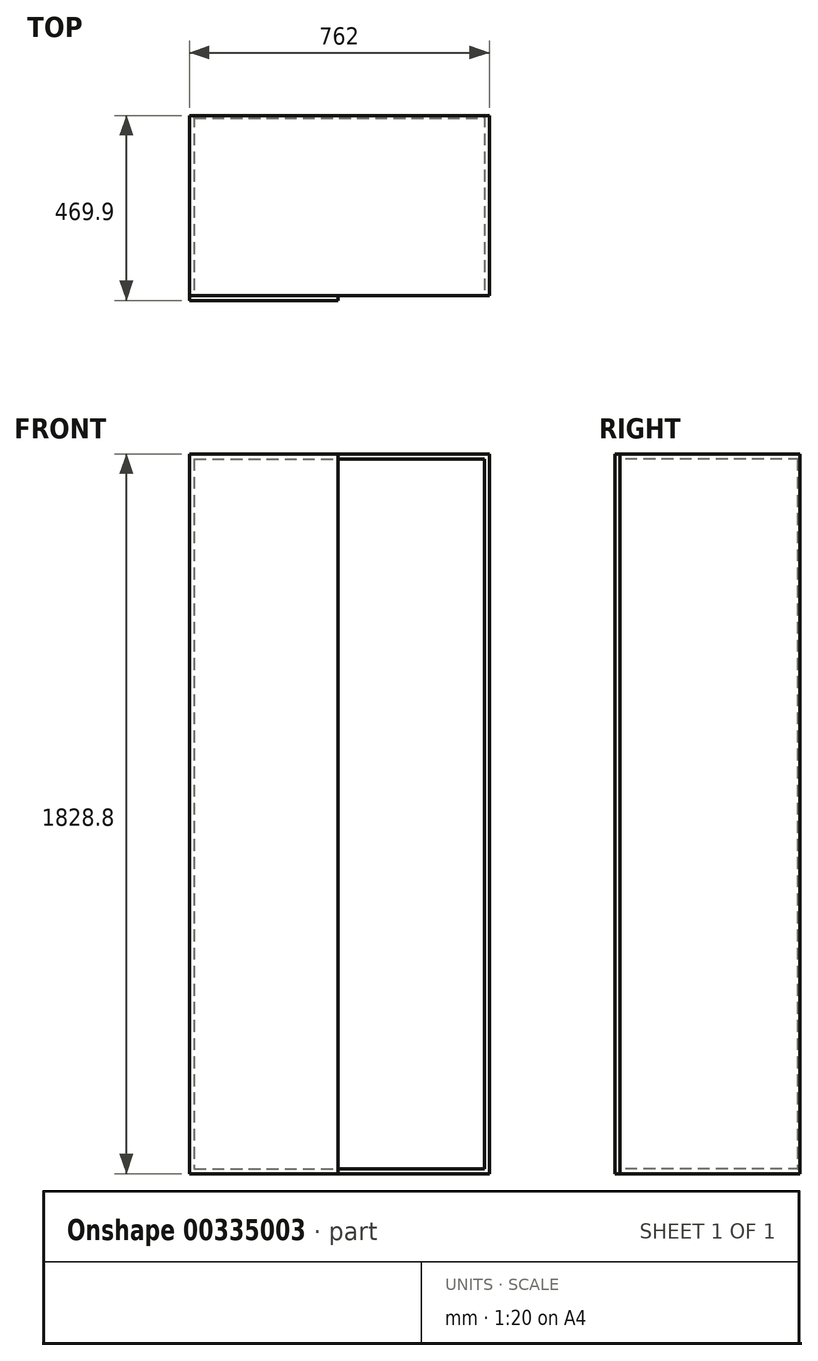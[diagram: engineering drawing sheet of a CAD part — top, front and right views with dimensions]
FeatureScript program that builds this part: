
annotation { "Feature Type Name" : "Feature", "Feature Type Description" : "" }
export const myFeature = defineFeature(function(context is Context, id is Id, definition is map)
    precondition{}
    {
        {
            var Q0;
            Q0=qCreatedBy(makeId("Front.planeOp"),FACE);
            var sketch = newSketch(context, id + "F0", { "sketchPlane" : qUnion([Q0])});
            skLineSegment(sketch, "E0.bottom", {"start": v(-381, 1828.8) * mm, "end": v(381, 1828.8) * mm});
            skLineSegment(sketch, "E0.top", {"start": v(-381, 0) * mm, "end": v(381, 0) * mm});
            skLineSegment(sketch, "E0.left", {"start": v(-381, 1828.8) * mm, "end": v(-381, 0) * mm});
            skLineSegment(sketch, "E0.right", {"start": v(381, 1828.8) * mm, "end": v(381, 0) * mm});
            skLineSegment(sketch, "E1.0", {"start": v(-368.3, 1816.1) * mm, "end": v(-368.3, 12.7) * mm});
            skLineSegment(sketch, "E1.1", {"start": v(-368.3, 1816.1) * mm, "end": v(368.3, 1816.1) * mm});
            skLineSegment(sketch, "E1.2", {"start": v(368.3, 1816.1) * mm, "end": v(368.3, 12.7) * mm});
            skLineSegment(sketch, "E1.3", {"start": v(-368.3, 12.7) * mm, "end": v(368.3, 12.7) * mm});
            skSolve(sketch);
        }
        {
            var Q0;
            Q0=makeQuery(id+"F0.imprint","IMPRINT",FACE,{"disambiguationData":[TD([[makeQuery(id+"F0.imprint","IMPRINT",EDGE,{"derivedFrom":sQuery(id+"F0.wireOp",EDGE,"E0.bottom")}),-1.0]])]});
            extrude(context, id + "F1", {"entities" : qUnion([Q0]), "oppositeDirection" : true, "depth" : 457.2 * mm});
        }
        {
            var Q0;
            Q0=makeQuery(id+"F1.opExtrude","CAP_FACE",FACE,{"disambiguationData":[OSD([sQuery(id+"F0.wireOp",EDGE,"E0.bottom"),sQuery(id+"F0.wireOp",EDGE,"E0.top"),sQuery(id+"F0.wireOp",EDGE,"E0.left"),sQuery(id+"F0.wireOp",EDGE,"E0.right"),sQuery(id+"F0.wireOp",EDGE,"E1.0"),sQuery(id+"F0.wireOp",EDGE,"E1.1"),sQuery(id+"F0.wireOp",EDGE,"E1.2"),sQuery(id+"F0.wireOp",EDGE,"E1.3")])],"isStart":false});
            var sketch = newSketch(context, id + "F2", { "sketchPlane" : qUnion([Q0])});
            skLineSegment(sketch, "E2.bottom", {"start": v(-368.3, 1816.1) * mm, "end": v(368.3, 1816.1) * mm});
            skLineSegment(sketch, "E2.top", {"start": v(-368.3, 12.7) * mm, "end": v(368.3, 12.7) * mm});
            skLineSegment(sketch, "E2.left", {"start": v(-368.3, 1816.1) * mm, "end": v(-368.3, 12.7) * mm});
            skLineSegment(sketch, "E2.right", {"start": v(368.3, 1816.1) * mm, "end": v(368.3, 12.7) * mm});
            skSolve(sketch);
        }
        {
            var Q0;
            Q0=makeQuery(id+"F2.imprint","IMPRINT",FACE,{"disambiguationData":[TD([[makeQuery(id+"F2.imprint","IMPRINT",EDGE,{"derivedFrom":sQuery(id+"F2.wireOp",EDGE,"E2.bottom")}),1.0]])]});
            extrude(context, id + "F3", {"entities" : qUnion([Q0]), "oppositeDirection" : true, "depth" : 6.35 * mm});
        }
        {
            var Q0;
            Q0=makeQuery(id+"F1.opExtrude","CAP_FACE",FACE,{"disambiguationData":[OSD([sQuery(id+"F0.wireOp",EDGE,"E0.bottom"),sQuery(id+"F0.wireOp",EDGE,"E0.top"),sQuery(id+"F0.wireOp",EDGE,"E0.left"),sQuery(id+"F0.wireOp",EDGE,"E0.right"),sQuery(id+"F0.wireOp",EDGE,"E1.0"),sQuery(id+"F0.wireOp",EDGE,"E1.1"),sQuery(id+"F0.wireOp",EDGE,"E1.2"),sQuery(id+"F0.wireOp",EDGE,"E1.3")])],"isStart":true});
            var sketch = newSketch(context, id + "F4", { "sketchPlane" : qUnion([Q0])});
            skLineSegment(sketch, "E3.bottom", {"start": v(-381, 1828.8) * mm, "end": v(-3.18, 1828.8) * mm});
            skLineSegment(sketch, "E3.top", {"start": v(-381, 0) * mm, "end": v(-3.18, 0) * mm});
            skLineSegment(sketch, "E3.left", {"start": v(-381, 1828.8) * mm, "end": v(-381, 0) * mm});
            skLineSegment(sketch, "E3.right", {"start": v(-3.18, 1828.8) * mm, "end": v(-3.18, 0) * mm});
            skSolve(sketch);
        }
        {
            var Q0;
            Q0=qSketchRegion(id+"F4",true);
            extrude(context, id + "F5", {"entities" : qUnion([Q0]), "depth" : 12.7 * mm});
        }
    });
